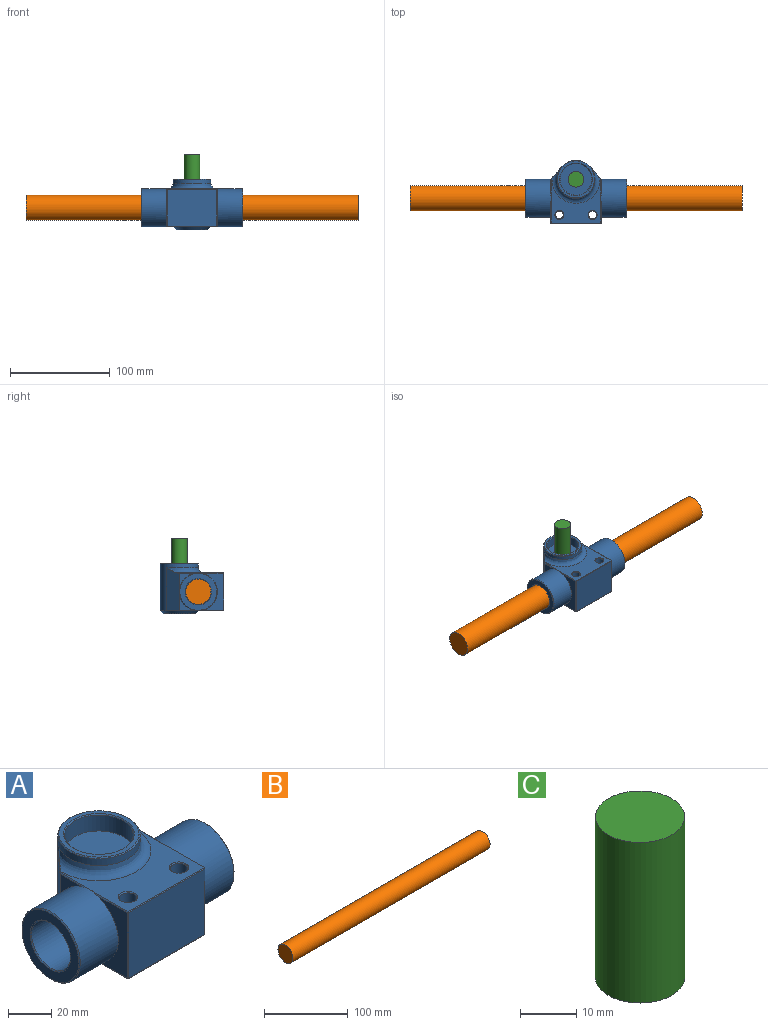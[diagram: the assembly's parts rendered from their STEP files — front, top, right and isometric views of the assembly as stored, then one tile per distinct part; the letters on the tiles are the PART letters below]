
ASSEMBLY  parts=3 mates=2
PART A: 65 faces, bbox 101.9x64.6x51.1 mm
  f0: plane 37.08x20.52mm, normal (-1,0,0), area 356mm2, adj f14,f40,f42,f47
  f1: plane 15.84x14.49mm, normal (-1,0,0), area 66.5mm2, adj f14,f43,f48
  f2: plane 15.84x14.49mm, normal (1,0,0), area 66.5mm2, adj f13,f27,f30
  f3: plane 37.08x20.52mm, normal (1,0,0), area 356mm2, adj f13,f32,f35,f36
  f4: plane 15.84x14.49mm, normal (-1,0,0), area 66.5mm2, adj f14,f48,f49
  f5: plane 49.78x37.08mm, normal (0,-1,0), area 1846.2mm2, adj f36,f37,f41,f42
  f6: plane 15.84x14.49mm, normal (1,0,0), area 66.5mm2, adj f13,f27,f33
  f7: plane 42.68x12.46mm, normal (0.75,0.66,0), area 648.5mm2, adj f8,f25,f26,f27,f29
  f8: cylinder r=19.05mm len=47.12mm, axis (0,0,-1), area 1868.7mm2, adj f7,f9,f23,f24,f25,f44,f56
  f9: plane 42.68x12.47mm, normal (-0.75,0.66,0), area 648.5mm2, adj f8,f44,f48,f50,f52
  f10: plane 49.78x44.63mm, normal (0,0,1), area 1145.7mm2, adj f24,f29,f33,f35,f41,f47,f49,f52
  f11: plane 52.93x49.78mm, normal (0,0,-1), area 1533.7mm2, adj f23,f25,f30,f32,f37,f40,f43,f44
  f12: plane 37.08x37.08mm, normal (1,0,0), area 532mm2, adj f57,f58
  f13: cylinder r=19.05mm len=38.1mm, axis (-1,0,0), area 2983.9mm2, adj f2,f3,f6,f27,f30,f32,f33,f35
  f14: cylinder r=19.05mm len=38.1mm, axis (-1,0,0), area 2983.9mm2, adj f0,f1,f4,f40,f43,f47,f48,f49
  f15: plane 37.08x37.08mm, normal (-1,0,0), area 532mm2, adj f53,f54
  f16: cylinder r=12.7mm len=100.58mm, axis (1,0,0), area 7932.7mm2, adj f53,f57,f60,f63
  f17: cylinder r=15.88mm len=31.75mm, axis (0,0,-1), area 899.4mm2, adj f19,f55
  f18: plane 37.08x37.08mm, normal (0,0,1), area 236.9mm2, adj f55,f56
  f19: plane 31.75x31.75mm, normal (0,0,1), area 791.7mm2, adj f17
  f20: plane 31.75x31.75mm, normal (0,0,-1), area 791.7mm2, adj f23
  f21: cylinder r=4mm len=37.08mm, axis (0,0,1), area 887.1mm2, adj f62,f63,f64
  f22: cylinder r=4mm len=37.08mm, axis (0,0,1), area 887.1mm2, adj f59,f60,f61
  f23: cone r=15.88mm half-angle=45deg, axis (0,0,1), area 492.7mm2, adj f8,f11,f20
  f24: torus R=24.13mm, axis (0,0,1), area 644.2mm2, adj f8,f10,f26,f50
  f25: plane 13.05x11.24mm, normal (0.53,0.47,-0.71), area 9.8mm2, adj f7,f8,f11,f28
  f26: bspline ~11.92x10.21mm, area 6.3mm2, adj f7,f24,f29
  f27: plane 37.23x0.48mm, normal (0.94,0.35,0), area 12.6mm2, adj f2,f6,f7,f13,f28,f31
  f28: plane 0.51x0.51mm, normal (0.68,0.26,-0.68), area 0.1mm2, adj f25,f27,f30
  f29: plane 1.21x1.15mm, normal (0.53,0.47,0.71), area 0.8mm2, adj f7,f10,f26,f31
  f30: plane 19.11x0.76mm, normal (0.71,0,-0.71), area 11.4mm2, adj f2,f11,f13,f28
  f31: plane 0.51x0.51mm, normal (0.68,0.26,0.68), area 0.1mm2, adj f27,f29,f33
  f32: plane 25.15x0.76mm, normal (0.71,0,-0.71), area 15.8mm2, adj f3,f11,f13,f34
  f33: plane 19.11x0.76mm, normal (0.71,0,0.71), area 11.4mm2, adj f6,f10,f13,f31
  f34: plane 0.51x0.51mm, normal (0.58,-0.58,-0.58), area 0.2mm2, adj f32,f36,f37
  f35: plane 25.15x0.76mm, normal (0.71,0,0.71), area 15.8mm2, adj f3,f10,f13,f38
  f36: plane 37.08x0.51mm, normal (0.71,-0.71,0), area 26.6mm2, adj f3,f5,f34,f38
  f37: plane 49.78x0.51mm, normal (0,-0.71,-0.71), area 35.8mm2, adj f5,f11,f34,f39
  f38: plane 0.51x0.51mm, normal (0.58,-0.58,0.58), area 0.2mm2, adj f35,f36,f41
  f39: plane 0.51x0.51mm, normal (-0.58,-0.58,-0.58), area 0.2mm2, adj f37,f40,f42
  f40: plane 25.15x0.76mm, normal (-0.71,0,-0.71), area 15.8mm2, adj f0,f11,f14,f39
  f41: plane 49.78x0.51mm, normal (0,-0.71,0.71), area 35.8mm2, adj f5,f10,f38,f45
  f42: plane 37.08x0.51mm, normal (-0.71,-0.71,0), area 26.6mm2, adj f0,f5,f39,f45
  f43: plane 19.11x0.76mm, normal (-0.71,0,-0.71), area 11.4mm2, adj f1,f11,f14,f46
  f44: plane 13.05x11.24mm, normal (-0.53,0.47,-0.71), area 9.8mm2, adj f8,f9,f11,f46
  f45: plane 0.51x0.51mm, normal (-0.58,-0.58,0.58), area 0.2mm2, adj f41,f42,f47
  f46: plane 0.51x0.51mm, normal (-0.68,0.26,-0.68), area 0.1mm2, adj f43,f44,f48
  f47: plane 25.15x0.76mm, normal (-0.71,0,0.71), area 15.8mm2, adj f0,f10,f14,f45
  f48: plane 37.23x0.48mm, normal (-0.94,0.35,0), area 12.6mm2, adj f1,f4,f9,f14,f46,f51
  f49: plane 19.11x0.76mm, normal (-0.71,0,0.71), area 11.4mm2, adj f4,f10,f14,f51
  f50: bspline ~11.92x10.21mm, area 6.3mm2, adj f9,f24,f52
  f51: plane 0.51x0.51mm, normal (-0.68,0.26,0.68), area 0.1mm2, adj f48,f49,f52
  f52: plane 1.21x1.15mm, normal (-0.53,0.47,0.71), area 0.8mm2, adj f9,f10,f50,f51
  f53: cone r=13.21mm half-angle=45deg, axis (-1,0,0), area 58.5mm2, adj f15,f16
  f54: cone r=19.05mm half-angle=45deg, axis (1,0,0), area 84.8mm2, adj f14,f15
  f55: cone r=15.88mm half-angle=45deg, axis (0,0,1), area 72.8mm2, adj f17,f18
  f56: cone r=18.54mm half-angle=45deg, axis (0,0,-1), area 84.8mm2, adj f8,f18
  f57: cone r=12.7mm half-angle=45deg, axis (1,0,0), area 58.5mm2, adj f12,f16
  f58: cone r=18.54mm half-angle=45deg, axis (-1,0,0), area 84.8mm2, adj f12,f13
  f59: cone r=4.51mm half-angle=45deg, axis (0,0,-1), area 19.2mm2, adj f11,f22
  f60: bspline ~10.3x5.77mm, area 24.9mm2, adj f16,f22
  f61: cone r=4mm half-angle=45deg, axis (0,0,1), area 19.2mm2, adj f10,f22
  f62: cone r=4.51mm half-angle=45deg, axis (0,0,-1), area 19.2mm2, adj f11,f21
  f63: bspline ~10.3x5.77mm, area 24.9mm2, adj f16,f21
  f64: cone r=4mm half-angle=45deg, axis (0,0,1), area 19.2mm2, adj f10,f21
PART B: 3 faces, bbox 333.4x25.4x25.4 mm
  f0: cylinder r=12.7mm len=333.38mm, axis (-1,0,0), area 26602.1mm2, adj f1,f2
  f1: plane 25.4x25.4mm, normal (1,0,0), area 506.7mm2, adj f0
  f2: plane 25.4x25.4mm, normal (-1,0,0), area 506.7mm2, adj f0
PART C: 3 faces, bbox 15.9x15.9x34.9 mm
  f0: cylinder r=7.94mm len=34.93mm, axis (0,0,-1), area 1741.8mm2, adj f1,f2
  f1: plane 15.88x15.88mm, normal (0,0,1), area 197.9mm2, adj f0
  f2: plane 15.88x15.88mm, normal (0,0,-1), area 197.9mm2, adj f0
PLACE A at identity fixed
PLACE B at identity
PLACE C rot(axis=(0,0,-1),90deg) t=(0,0,0)mm
MATE revolute C.f0 <-> A.f8  axis (0,0,-1) through (0,0,19.05)mm
MATE cylindrical B.f0 <-> A.f13  axis (-1,0,0) through (0,-19.05,0)mm
